# Revit family: Shower_Holder-GROHE-Relexa-28622_Series
name_source: partatom
category: Pipe Accessories
revit_build: Autodesk Revit 2014 (Build: 20130308_1515(x64)
units: mm (PartAtom-declared; Revit-internal decimal feet)

## types (2) — shared parameters
Assembly Code = D2090800
Default Elevation = 0"
Description = Relexa Wall Hand Shower Holder
Height = 2 9/16"
Installation Type = Wall Mounted
Manufacturer = Grohe
Price = Prices may vary. Please consult Manufacturer Representative for most up-to-date price list.
Product Page URL = https://www.grohe.us
URL = https://www.grohe.us
Warranty Documentation Link = https://cdn.cloud.grohe.com
Width = 1 23/32"

## per-type parameters (varying)
| type | Finish | Material |
| 28622000 | Metal-Grohe-000-Chrome | Metal-Grohe-000-Chrome |
| 28622EN0 | Metal-Grohe-EN0-Brushed Nickel | Metal-Grohe-EN0-Brushed Nickel |

note: column(s) folded — value = type name in every type: Model

## geometry (parser evidence)
native form markers: Sweep x3
no freeform markers — native parametric forms only
